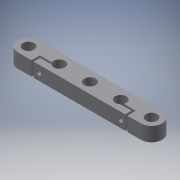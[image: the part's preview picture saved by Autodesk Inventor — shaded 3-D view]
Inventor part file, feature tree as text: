
AUTODESK INVENTOR PART (.ipt)
format: ipt  version: 2016 (Build 200138000, 138)  size: 184,832 bytes
history: native  units: mm
features: extrude x4, sketch x4, mirror x1, projected_geometry x1
ambient origin geometry x8: Origin, YZ Plane, XZ Plane, XY Plane, X Axis, Y Axis, Z Axis, Center Point
bodies: Solid1 (feature_tree)
feature tree (10):
  extrude  "Extrusion1"  Depth=8.0mm
  extrude  "Extrusion2"  Depth=10.0mm TaperAngle=0.0deg
  extrude  "Extrusion3"  Depth=1.5mm
  extrude  "Extrusion4"  Depth=10.0mm TaperAngle=0.0deg
  mirror  "Mirror1"
  sketch  "Sketch1"  dims[d1=8.0mm d2=8.0mm]
  sketch  "Sketch2"  dims[d4=15.0mm d5=10.0mm d6=0.0mm]
  sketch  "Sketch3"  dims[d7=1.5mm d8=8.0mm]
  projected_geometry  "Projected Loop1"
  sketch  "Sketch4"  dims[d9=1.5mm d10=10.0mm d11=0.0mm d12=3.5mm d13=10.0mm d14=0.0mm d15=5.6mm d16=3.0mm d17=0.0mm d18=1.0mm d19=43.5mm d22=22.0mm]
